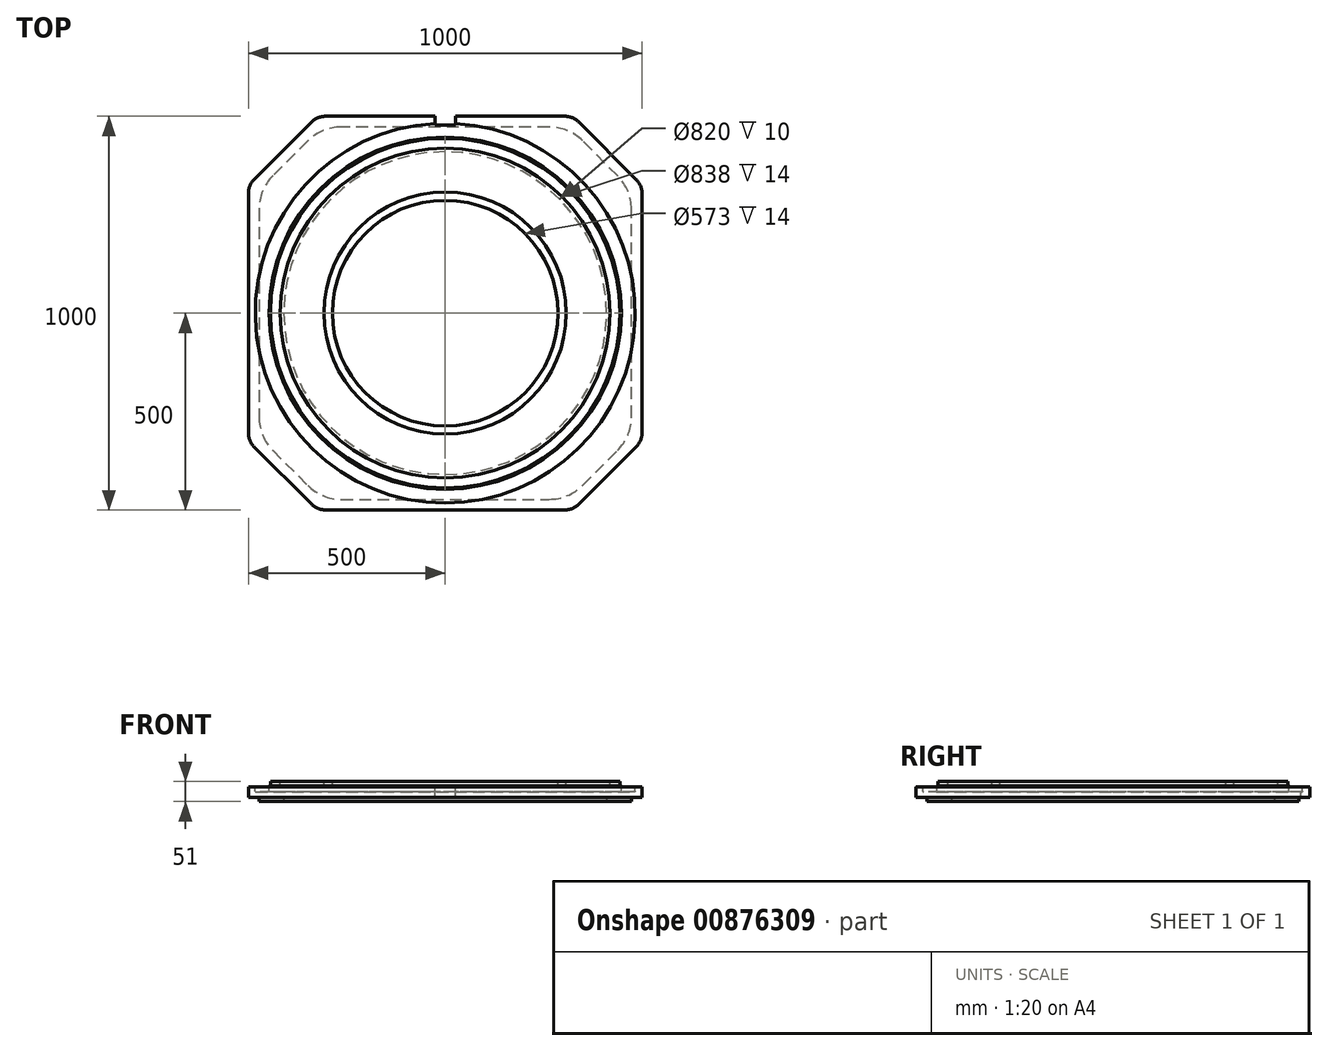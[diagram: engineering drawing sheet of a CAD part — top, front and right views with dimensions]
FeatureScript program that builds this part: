
annotation { "Feature Type Name" : "Feature", "Feature Type Description" : "" }
export const myFeature = defineFeature(function(context is Context, id is Id, definition is map)
    precondition{}
    {
        {
            var Q0;
            Q0=qCreatedBy(makeId("Top.planeOp"),FACE);
            var sketch = newSketch(context, id + "F0", { "sketchPlane" : qUnion([Q0])});
            skLineSegment(sketch, "E0.bottom", {"start": v(-500, 500) * mm, "end": v(500, 500) * mm});
            skLineSegment(sketch, "E0.top", {"start": v(-500, -500) * mm, "end": v(500, -500) * mm});
            skLineSegment(sketch, "E0.left", {"start": v(-500, 500) * mm, "end": v(-500, -500) * mm});
            skLineSegment(sketch, "E0.right", {"start": v(500, 500) * mm, "end": v(500, -500) * mm});
            skSolve(sketch);
        }
        {
            var Q0;
            Q0 = qSketchRegion(id + "F0", true);
            extrude(context, id + "F1", {"entities" : qUnion([Q0]), "depth" : 51 * mm, "offsetDistance" : 25 * mm});
        }
        {
            var Q0;
            Q0=makeQuery(id+"F1.opExtrude","SWEPT_EDGE",EDGE,{"disambiguationData":[OSD([sQuery(id+"F0.wireOp",EDGE,"E0.top"),sQuery(id+"F0.wireOp",EDGE,"E0.left")])]});
            var Q1;
            Q1=makeQuery(id+"F1.opExtrude","SWEPT_EDGE",EDGE,{"disambiguationData":[OSD([sQuery(id+"F0.wireOp",EDGE,"E0.top"),sQuery(id+"F0.wireOp",EDGE,"E0.right")])]});
            var Q2;
            Q2=makeQuery(id+"F1.opExtrude","SWEPT_EDGE",EDGE,{"disambiguationData":[OSD([sQuery(id+"F0.wireOp",EDGE,"E0.bottom"),sQuery(id+"F0.wireOp",EDGE,"E0.right")])]});
            var Q3;
            Q3=makeQuery(id+"F1.opExtrude","SWEPT_EDGE",EDGE,{"disambiguationData":[OSD([sQuery(id+"F0.wireOp",EDGE,"E0.bottom"),sQuery(id+"F0.wireOp",EDGE,"E0.left")])]});
            chamfer(context, id + "F2", {"entities" : qUnion([Q0, Q1, Q2, Q3]), "width" : 175 * mm, "tangentPropagation" : true});
        }
        {
            var Q0;
            {var subQ0=sQuery(id+"F0.wireOp",EDGE,"E0.left");Q0=makeQuery(id+"F2.opChamfer","BLEND_EDGE",EDGE,{"blendedFrom":[makeQuery(id+"F1.opExtrude","SWEPT_EDGE",EDGE,{"disambiguationData":[OSD([sQuery(id+"F0.wireOp",EDGE,"E0.top"),subQ0])]}),makeQuery(id+"F1.opExtrude","SWEPT_FACE",FACE,{"disambiguationData":[OSD([subQ0])]})],"blendedInto":[makeQuery(id+"F1.opExtrude","SWEPT_FACE",FACE,{"disambiguationData":[OSD([subQ0])]})]});}
            var Q1;
            {var subQ0=sQuery(id+"F0.wireOp",EDGE,"E0.top");Q1=makeQuery(id+"F2.opChamfer","BLEND_EDGE",EDGE,{"blendedFrom":[makeQuery(id+"F1.opExtrude","SWEPT_EDGE",EDGE,{"disambiguationData":[OSD([subQ0,sQuery(id+"F0.wireOp",EDGE,"E0.left")])]}),makeQuery(id+"F1.opExtrude","SWEPT_FACE",FACE,{"disambiguationData":[OSD([subQ0])]})],"blendedInto":[makeQuery(id+"F1.opExtrude","SWEPT_FACE",FACE,{"disambiguationData":[OSD([subQ0])]})]});}
            var Q2;
            {var subQ0=sQuery(id+"F0.wireOp",EDGE,"E0.top");Q2=makeQuery(id+"F2.opChamfer","BLEND_EDGE",EDGE,{"blendedFrom":[makeQuery(id+"F1.opExtrude","SWEPT_EDGE",EDGE,{"disambiguationData":[OSD([subQ0,sQuery(id+"F0.wireOp",EDGE,"E0.right")])]}),makeQuery(id+"F1.opExtrude","SWEPT_FACE",FACE,{"disambiguationData":[OSD([subQ0])]})],"blendedInto":[makeQuery(id+"F1.opExtrude","SWEPT_FACE",FACE,{"disambiguationData":[OSD([subQ0])]})]});}
            var Q3;
            {var subQ0=sQuery(id+"F0.wireOp",EDGE,"E0.right");Q3=makeQuery(id+"F2.opChamfer","BLEND_EDGE",EDGE,{"blendedFrom":[makeQuery(id+"F1.opExtrude","SWEPT_EDGE",EDGE,{"disambiguationData":[OSD([sQuery(id+"F0.wireOp",EDGE,"E0.top"),subQ0])]}),makeQuery(id+"F1.opExtrude","SWEPT_FACE",FACE,{"disambiguationData":[OSD([subQ0])]})],"blendedInto":[makeQuery(id+"F1.opExtrude","SWEPT_FACE",FACE,{"disambiguationData":[OSD([subQ0])]})]});}
            var Q4;
            {var subQ0=sQuery(id+"F0.wireOp",EDGE,"E0.left");Q4=makeQuery(id+"F2.opChamfer","BLEND_EDGE",EDGE,{"blendedFrom":[makeQuery(id+"F1.opExtrude","SWEPT_EDGE",EDGE,{"disambiguationData":[OSD([sQuery(id+"F0.wireOp",EDGE,"E0.bottom"),subQ0])]}),makeQuery(id+"F1.opExtrude","SWEPT_FACE",FACE,{"disambiguationData":[OSD([subQ0])]})],"blendedInto":[makeQuery(id+"F1.opExtrude","SWEPT_FACE",FACE,{"disambiguationData":[OSD([subQ0])]})]});}
            var Q5;
            {var subQ0=sQuery(id+"F0.wireOp",EDGE,"E0.right");Q5=makeQuery(id+"F2.opChamfer","BLEND_EDGE",EDGE,{"blendedFrom":[makeQuery(id+"F1.opExtrude","SWEPT_EDGE",EDGE,{"disambiguationData":[OSD([sQuery(id+"F0.wireOp",EDGE,"E0.bottom"),subQ0])]}),makeQuery(id+"F1.opExtrude","SWEPT_FACE",FACE,{"disambiguationData":[OSD([subQ0])]})],"blendedInto":[makeQuery(id+"F1.opExtrude","SWEPT_FACE",FACE,{"disambiguationData":[OSD([subQ0])]})]});}
            var Q6;
            {var subQ0=sQuery(id+"F0.wireOp",EDGE,"E0.bottom");Q6=makeQuery(id+"F2.opChamfer","BLEND_EDGE",EDGE,{"blendedFrom":[makeQuery(id+"F1.opExtrude","SWEPT_EDGE",EDGE,{"disambiguationData":[OSD([subQ0,sQuery(id+"F0.wireOp",EDGE,"E0.right")])]}),makeQuery(id+"F1.opExtrude","SWEPT_FACE",FACE,{"disambiguationData":[OSD([subQ0])]})],"blendedInto":[makeQuery(id+"F1.opExtrude","SWEPT_FACE",FACE,{"disambiguationData":[OSD([subQ0])]})]});}
            var Q7;
            {var subQ0=sQuery(id+"F0.wireOp",EDGE,"E0.bottom");Q7=makeQuery(id+"F2.opChamfer","BLEND_EDGE",EDGE,{"blendedFrom":[makeQuery(id+"F1.opExtrude","SWEPT_EDGE",EDGE,{"disambiguationData":[OSD([subQ0,sQuery(id+"F0.wireOp",EDGE,"E0.left")])]}),makeQuery(id+"F1.opExtrude","SWEPT_FACE",FACE,{"disambiguationData":[OSD([subQ0])]})],"blendedInto":[makeQuery(id+"F1.opExtrude","SWEPT_FACE",FACE,{"disambiguationData":[OSD([subQ0])]})]});}
            fillet(context, id + "F3", {"entities" : qUnion([Q0, Q1, Q2, Q3, Q4, Q5, Q6, Q7]), "radius" : 50 * mm, "tangentPropagation" : true, "allowEdgeOverflow" : false});
        }
        {
            var Q0;
            Q0=qCreatedBy(makeId("Front.planeOp"),FACE);
            var sketch = newSketch(context, id + "F4", { "sketchPlane" : qUnion([Q0])});
            skLineSegment(sketch, "E1", {"start": v(0, 0) * mm, "end": v(0, 174.91) * mm, "construction": true});
            skSolve(sketch);
        }
        {
            var Q0;
            Q0=makeQuery(id+"F1.opExtrude","CAP_FACE",FACE,{"disambiguationData":[OSD([sQuery(id+"F0.wireOp",EDGE,"E0.bottom"),sQuery(id+"F0.wireOp",EDGE,"E0.top"),sQuery(id+"F0.wireOp",EDGE,"E0.left"),sQuery(id+"F0.wireOp",EDGE,"E0.right")])],"isStart":false});
            var sketch = newSketch(context, id + "F5", { "sketchPlane" : qUnion([Q0])});
            skLineSegment(sketch, "E2.bottom", {"start": v(-26, 578) * mm, "end": v(26, 578) * mm});
            skLineSegment(sketch, "E2.top", {"start": v(-26, 478) * mm, "end": v(26, 478) * mm});
            skLineSegment(sketch, "E2.left", {"start": v(-26, 578) * mm, "end": v(-26, 478) * mm});
            skLineSegment(sketch, "E2.right", {"start": v(26, 578) * mm, "end": v(26, 478) * mm});
            skSolve(sketch);
        }
        {
            var Q0;
            Q0 = qSketchRegion(id + "F5", true);
            extrude(context, id + "F6", {"entities" : qUnion([Q0]), "operationType" : NewBodyOperationType.REMOVE, "oppositeDirection" : true, "depth" : 100 * mm, "offsetDistance" : 25 * mm});
        }
        {
            var Q0;
            Q0=qCreatedBy(makeId("Top.planeOp"),FACE);
            var sketch = newSketch(context, id + "F7", { "sketchPlane" : qUnion([Q0])});
            skCircle(sketch, "E3", {"center": v(0, 0) * mm, "radius": 410 * mm});
            skSolve(sketch);
        }
        {
            var Q0;
            Q0 = qSketchRegion(id + "F7", true);
            extrude(context, id + "F8", {"entities" : qUnion([Q0]), "operationType" : NewBodyOperationType.REMOVE, "depth" : 10 * mm, "offsetDistance" : 25 * mm});
        }
        {
            var Q0;
            Q0=qCreatedBy(makeId("Top.planeOp"),FACE);
            var sketch = newSketch(context, id + "F9", { "sketchPlane" : qUnion([Q0])});
            skLineSegment(sketch, "E4", {"start": v(473, -313.82) * mm, "end": v(473, 313.82) * mm});
            skLineSegment(sketch, "E5", {"start": v(473, 313.82) * mm, "end": v(313.82, 473) * mm});
            skLineSegment(sketch, "E6", {"start": v(313.82, 473) * mm, "end": v(-313.82, 473) * mm});
            skLineSegment(sketch, "E7", {"start": v(-313.82, 473) * mm, "end": v(-473, 313.82) * mm});
            skLineSegment(sketch, "E8", {"start": v(-473, 313.82) * mm, "end": v(-473, -313.82) * mm});
            skLineSegment(sketch, "E9", {"start": v(-473, -313.82) * mm, "end": v(-313.82, -473) * mm});
            skLineSegment(sketch, "E10", {"start": v(-313.82, -473) * mm, "end": v(313.82, -473) * mm});
            skLineSegment(sketch, "E11", {"start": v(313.82, -473) * mm, "end": v(473, -313.82) * mm});
            skLineSegment(sketch, "E12.bottom", {"start": v(635.7, -615.2) * mm, "end": v(-696.39, -615.2) * mm});
            skLineSegment(sketch, "E12.top", {"start": v(635.7, 774.71) * mm, "end": v(-696.39, 774.71) * mm});
            skLineSegment(sketch, "E12.left", {"start": v(635.7, -615.2) * mm, "end": v(635.7, 774.71) * mm});
            skLineSegment(sketch, "E12.right", {"start": v(-696.39, -615.2) * mm, "end": v(-696.39, 774.71) * mm});
            skSolve(sketch);
        }
        {
            var Q0;
            Q0 = qSketchRegion(id + "F9", true);
            extrude(context, id + "F10", {"entities" : qUnion([Q0]), "operationType" : NewBodyOperationType.REMOVE, "depth" : 10 * mm, "offsetDistance" : 25 * mm});
        }
        {
            var Q0;
            Q0=makeQuery(id+"F10.boolean.opBoolean","COPY",EDGE,{"derivedFrom":makeQuery(id+"F10.opExtrude","SWEPT_EDGE",EDGE,{"disambiguationData":[OSD([sQuery(id+"F9.wireOp",EDGE,"E9"),sQuery(id+"F9.wireOp",EDGE,"E10")])]})});
            var Q1;
            Q1=makeQuery(id+"F10.boolean.opBoolean","COPY",EDGE,{"derivedFrom":makeQuery(id+"F10.opExtrude","SWEPT_EDGE",EDGE,{"disambiguationData":[OSD([sQuery(id+"F9.wireOp",EDGE,"E8"),sQuery(id+"F9.wireOp",EDGE,"E9")])]})});
            var Q2;
            Q2=makeQuery(id+"F10.boolean.opBoolean","COPY",EDGE,{"derivedFrom":makeQuery(id+"F10.opExtrude","SWEPT_EDGE",EDGE,{"disambiguationData":[OSD([sQuery(id+"F9.wireOp",EDGE,"E7"),sQuery(id+"F9.wireOp",EDGE,"E8")])]})});
            var Q3;
            Q3=makeQuery(id+"F10.boolean.opBoolean","COPY",EDGE,{"derivedFrom":makeQuery(id+"F10.opExtrude","SWEPT_EDGE",EDGE,{"disambiguationData":[OSD([sQuery(id+"F9.wireOp",EDGE,"E6"),sQuery(id+"F9.wireOp",EDGE,"E7")])]})});
            var Q4;
            Q4=makeQuery(id+"F10.boolean.opBoolean","COPY",EDGE,{"derivedFrom":makeQuery(id+"F10.opExtrude","SWEPT_EDGE",EDGE,{"disambiguationData":[OSD([sQuery(id+"F9.wireOp",EDGE,"E4"),sQuery(id+"F9.wireOp",EDGE,"E11")])]})});
            var Q5;
            Q5=makeQuery(id+"F10.boolean.opBoolean","COPY",EDGE,{"derivedFrom":makeQuery(id+"F10.opExtrude","SWEPT_EDGE",EDGE,{"disambiguationData":[OSD([sQuery(id+"F9.wireOp",EDGE,"E10"),sQuery(id+"F9.wireOp",EDGE,"E11")])]})});
            var Q6;
            Q6=makeQuery(id+"F10.boolean.opBoolean","COPY",EDGE,{"derivedFrom":makeQuery(id+"F10.opExtrude","SWEPT_EDGE",EDGE,{"disambiguationData":[OSD([sQuery(id+"F9.wireOp",EDGE,"E5"),sQuery(id+"F9.wireOp",EDGE,"E6")])]})});
            var Q7;
            Q7=makeQuery(id+"F10.boolean.opBoolean","COPY",EDGE,{"derivedFrom":makeQuery(id+"F10.opExtrude","SWEPT_EDGE",EDGE,{"disambiguationData":[OSD([sQuery(id+"F9.wireOp",EDGE,"E4"),sQuery(id+"F9.wireOp",EDGE,"E5")])]})});
            fillet(context, id + "F11", {"entities" : qUnion([Q0, Q1, Q2, Q3, Q4, Q5, Q6, Q7]), "radius" : 120 * mm, "tangentPropagation" : true, "allowEdgeOverflow" : false});
        }
        {
            var Q0;
            Q0=makeQuery(id+"F1.opExtrude","CAP_FACE",FACE,{"disambiguationData":[OSD([sQuery(id+"F0.wireOp",EDGE,"E0.bottom"),sQuery(id+"F0.wireOp",EDGE,"E0.top"),sQuery(id+"F0.wireOp",EDGE,"E0.left"),sQuery(id+"F0.wireOp",EDGE,"E0.right")])],"isStart":false});
            var sketch = newSketch(context, id + "F12", { "sketchPlane" : qUnion([Q0])});
            skCircle(sketch, "E13", {"center": v(0, 0) * mm, "radius": 700 * mm});
            skCircle(sketch, "E14", {"center": v(0, 0) * mm, "radius": 444 * mm});
            skSolve(sketch);
        }
        {
            var Q0;
            Q0 = qSketchRegion(id + "F12", true);
            extrude(context, id + "F13", {"entities" : qUnion([Q0]), "operationType" : NewBodyOperationType.REMOVE, "oppositeDirection" : true, "depth" : 11 * mm, "offsetDistance" : 25 * mm});
        }
        {
            var Q0;
            Q0=makeQuery(id+"F1.opExtrude","CAP_FACE",FACE,{"disambiguationData":[OSD([sQuery(id+"F0.wireOp",EDGE,"E0.bottom"),sQuery(id+"F0.wireOp",EDGE,"E0.top"),sQuery(id+"F0.wireOp",EDGE,"E0.left"),sQuery(id+"F0.wireOp",EDGE,"E0.right")])],"isStart":false});
            var sketch = newSketch(context, id + "F14", { "sketchPlane" : qUnion([Q0])});
            skCircle(sketch, "E15", {"center": v(0, 0) * mm, "radius": 700 * mm});
            skCircle(sketch, "E16", {"center": v(0, 0) * mm, "radius": 447.5 * mm});
            skSolve(sketch);
        }
        {
            var Q0;
            Q0 = qSketchRegion(id + "F14", true);
            extrude(context, id + "F15", {"entities" : qUnion([Q0]), "operationType" : NewBodyOperationType.REMOVE, "oppositeDirection" : true, "depth" : 14 * mm, "offsetDistance" : 25 * mm});
        }
        {
            var Q0;
            Q0=makeQuery(id+"F1.opExtrude","CAP_FACE",FACE,{"disambiguationData":[OSD([sQuery(id+"F0.wireOp",EDGE,"E0.bottom"),sQuery(id+"F0.wireOp",EDGE,"E0.top"),sQuery(id+"F0.wireOp",EDGE,"E0.left"),sQuery(id+"F0.wireOp",EDGE,"E0.right")])],"isStart":false});
            var sketch = newSketch(context, id + "F16", { "sketchPlane" : qUnion([Q0])});
            skCircle(sketch, "E17.0", {"center": v(0, 0) * mm, "radius": 447.5 * mm});
            skCircle(sketch, "E18", {"center": v(0, 0) * mm, "radius": 482.5 * mm});
            skSolve(sketch);
        }
        {
            var Q0;
            Q0 = qSketchRegion(id + "F16", true);
            extrude(context, id + "F17", {"entities" : qUnion([Q0]), "operationType" : NewBodyOperationType.REMOVE, "oppositeDirection" : true, "depth" : 26 * mm, "offsetDistance" : 25 * mm});
        }
        {
            var Q0;
            {var subQ0=sQuery(id+"F16.wireOp",EDGE,"E18");Q0=makeQuery(id+"F17.boolean.opBoolean","COPY",EDGE,{"disambiguationData":[TD([makeQuery(id+"F6.boolean.opBoolean","COPY",FACE,{"derivedFrom":makeQuery(id+"F6.opExtrude","SWEPT_FACE",FACE,{"disambiguationData":[OSD([sQuery(id+"F5.wireOp",EDGE,"E2.left")])]})})])],"derivedFrom":makeQuery(id+"F17.opExtrude","CAP_EDGE",EDGE,{"disambiguationData":[OSD([subQ0])],"isStart":false})});}
            var Q1;
            {var subQ0=sQuery(id+"F16.wireOp",EDGE,"E18");Q1=makeQuery(id+"F17.boolean.opBoolean","COPY",EDGE,{"disambiguationData":[TD([makeQuery(id+"FaierujuCbJv55j_1.1.F6.boolean.opBoolean","COPY",FACE,{"derivedFrom":makeQuery(id+"FaierujuCbJv55j_1.1.F6.opExtrude","SWEPT_FACE",FACE,{"disambiguationData":[OSD([sQuery(id+"F5.wireOp",EDGE,"E2.left")])]})})])],"derivedFrom":makeQuery(id+"F17.opExtrude","CAP_EDGE",EDGE,{"disambiguationData":[OSD([subQ0])],"isStart":false})});}
            var Q2;
            {var subQ0=sQuery(id+"F16.wireOp",EDGE,"E18");Q2=makeQuery(id+"F17.boolean.opBoolean","COPY",EDGE,{"disambiguationData":[TD([makeQuery(id+"F6.boolean.opBoolean","COPY",FACE,{"derivedFrom":makeQuery(id+"F6.opExtrude","SWEPT_FACE",FACE,{"disambiguationData":[OSD([sQuery(id+"F5.wireOp",EDGE,"E2.right")])]})})])],"derivedFrom":makeQuery(id+"F17.opExtrude","CAP_EDGE",EDGE,{"disambiguationData":[OSD([subQ0])],"isStart":false})});}
            var Q3;
            {var subQ0=sQuery(id+"F16.wireOp",EDGE,"E18");Q3=makeQuery(id+"F17.boolean.opBoolean","COPY",EDGE,{"disambiguationData":[TD([makeQuery(id+"FaierujuCbJv55j_1.2.F6.boolean.opBoolean","COPY",FACE,{"derivedFrom":makeQuery(id+"FaierujuCbJv55j_1.2.F6.opExtrude","SWEPT_FACE",FACE,{"disambiguationData":[OSD([sQuery(id+"F5.wireOp",EDGE,"E2.left")])]})})])],"derivedFrom":makeQuery(id+"F17.opExtrude","CAP_EDGE",EDGE,{"disambiguationData":[OSD([subQ0])],"isStart":false})});}
            var Q4;
            Q4=makeQuery(id+"F17.boolean.opBoolean","COPY",EDGE,{"derivedFrom":makeQuery(id+"F17.opExtrude","CAP_EDGE",EDGE,{"disambiguationData":[OSD([sQuery(id+"F16.wireOp",EDGE,"E17.0")])],"isStart":false})});
            var Q5;
            Q5=makeQuery(id+"F13.boolean.opBoolean","COPY",EDGE,{"derivedFrom":makeQuery(id+"F13.opExtrude","CAP_EDGE",EDGE,{"disambiguationData":[OSD([sQuery(id+"F12.wireOp",EDGE,"E14")])],"isStart":false})});
            var Q6;
            Q6=makeQuery(id+"F15.boolean.opBoolean","INTERSECT",EDGE,{"derivedFrom":[makeQuery(id+"F13.boolean.opBoolean","COPY",FACE,{"derivedFrom":makeQuery(id+"F13.opExtrude","CAP_FACE",FACE,{"disambiguationData":[OSD([sQuery(id+"F12.wireOp",EDGE,"E13"),sQuery(id+"F12.wireOp",EDGE,"E14")])],"isStart":false})}),makeQuery(id+"F15.opExtrude","SWEPT_FACE",FACE,{"disambiguationData":[OSD([sQuery(id+"F14.wireOp",EDGE,"E16")])]})]});
            var Q7;
            Q7=makeQuery(id+"F13.boolean.opBoolean","COPY",EDGE,{"derivedFrom":makeQuery(id+"F13.opExtrude","CAP_EDGE",EDGE,{"disambiguationData":[OSD([sQuery(id+"F12.wireOp",EDGE,"E14")])],"isStart":true})});
            fillet(context, id + "F18", {"entities" : qUnion([Q0, Q1, Q2, Q3, Q4, Q5, Q6, Q7]), "radius" : 1 * mm, "tangentPropagation" : true, "allowEdgeOverflow" : false});
        }
        {
            var Q0;
            Q0=makeQuery(id+"F1.opExtrude","CAP_FACE",FACE,{"disambiguationData":[OSD([sQuery(id+"F0.wireOp",EDGE,"E0.bottom"),sQuery(id+"F0.wireOp",EDGE,"E0.top"),sQuery(id+"F0.wireOp",EDGE,"E0.left"),sQuery(id+"F0.wireOp",EDGE,"E0.right")])],"isStart":false});
            var sketch = newSketch(context, id + "F19", { "sketchPlane" : qUnion([Q0])});
            skCircle(sketch, "E19", {"center": v(0, 0) * mm, "radius": 419 * mm});
            skCircle(sketch, "E20", {"center": v(0, 0) * mm, "radius": 307.5 * mm});
            skSolve(sketch);
        }
        {
            var Q0;
            Q0 = qSketchRegion(id + "F19", true);
            extrude(context, id + "F20", {"entities" : qUnion([Q0]), "operationType" : NewBodyOperationType.REMOVE, "oppositeDirection" : true, "depth" : 14 * mm, "offsetDistance" : 25 * mm});
        }
        {
            var Q0;
            Q0=makeQuery(id+"F20.boolean.opBoolean","SPLIT",FACE,{"disambiguationData":[TD([makeQuery(id+"F20.opExtrude","SWEPT_FACE",FACE,{"disambiguationData":[OSD([sQuery(id+"F19.wireOp",EDGE,"E20")])]})])],"derivedFrom":makeQuery(id+"F1.opExtrude","CAP_FACE",FACE,{"disambiguationData":[OSD([sQuery(id+"F0.wireOp",EDGE,"E0.bottom"),sQuery(id+"F0.wireOp",EDGE,"E0.top"),sQuery(id+"F0.wireOp",EDGE,"E0.left"),sQuery(id+"F0.wireOp",EDGE,"E0.right")])],"isStart":false})});
            var sketch = newSketch(context, id + "F21", { "sketchPlane" : qUnion([Q0])});
            skCircle(sketch, "E21", {"center": v(0, 0) * mm, "radius": 286.5 * mm});
            skSolve(sketch);
        }
        {
            var Q0;
            Q0 = qSketchRegion(id + "F21", true);
            extrude(context, id + "F22", {"entities" : qUnion([Q0]), "operationType" : NewBodyOperationType.REMOVE, "oppositeDirection" : true, "depth" : 14 * mm, "offsetDistance" : 25 * mm});
        }
    });
